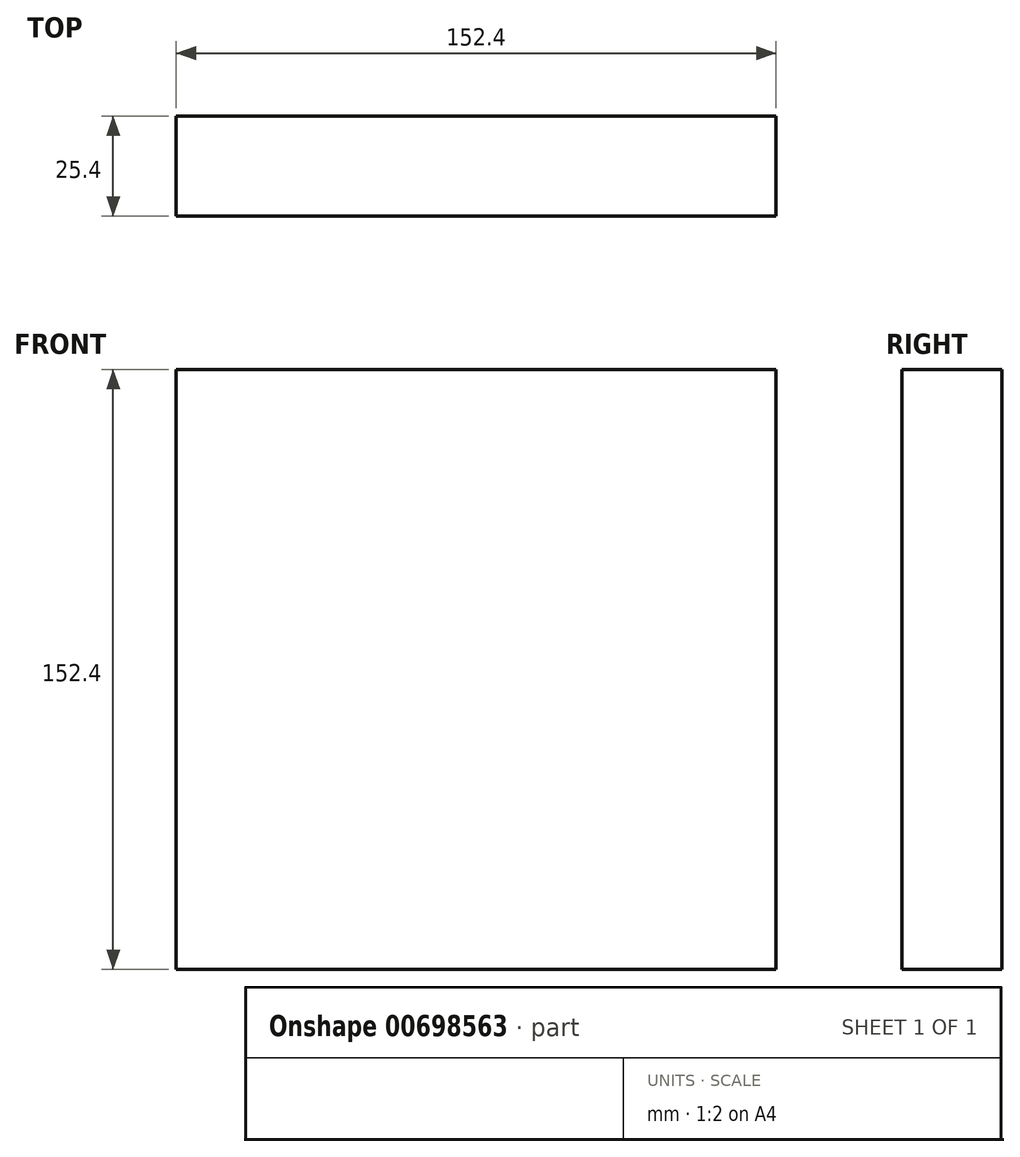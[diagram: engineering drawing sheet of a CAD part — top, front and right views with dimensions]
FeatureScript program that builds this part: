
annotation { "Feature Type Name" : "Feature", "Feature Type Description" : "" }
export const myFeature = defineFeature(function(context is Context, id is Id, definition is map)
    precondition{}
    {
        {
            var Q0;
            Q0=qCreatedBy(makeId("Front.planeOp"),FACE);
            var sketch = newSketch(context, id + "F0", { "sketchPlane" : qUnion([Q0])});
            skLineSegment(sketch, "E0.bottom", {"start": v(-160.52, -44.99) * mm, "end": v(-8.12, -44.99) * mm});
            skLineSegment(sketch, "E0.top", {"start": v(-160.52, 107.41) * mm, "end": v(-8.12, 107.41) * mm});
            skLineSegment(sketch, "E0.left", {"start": v(-160.52, -44.99) * mm, "end": v(-160.52, 107.41) * mm});
            skLineSegment(sketch, "E0.right", {"start": v(-8.12, -44.99) * mm, "end": v(-8.12, 107.41) * mm});
            skSolve(sketch);
        }
        {
            var Q0;
            Q0 = qSketchRegion(id + "F0", true);
            var Q1;
            Q1=makeQuery(id+"F0.imprint","IMPRINT",FACE,{"disambiguationData":[TD([[makeQuery(id+"F0.imprint","IMPRINT",EDGE,{"derivedFrom":sQuery(id+"F0.wireOp",EDGE,"E0.bottom")}),1.0]])]});
            extrude(context, id + "F1", {"entities" : qUnion([Q0, Q1]), "depth" : 25.4 * mm, "offsetDistance" : 25.4 * mm});
        }
    });
